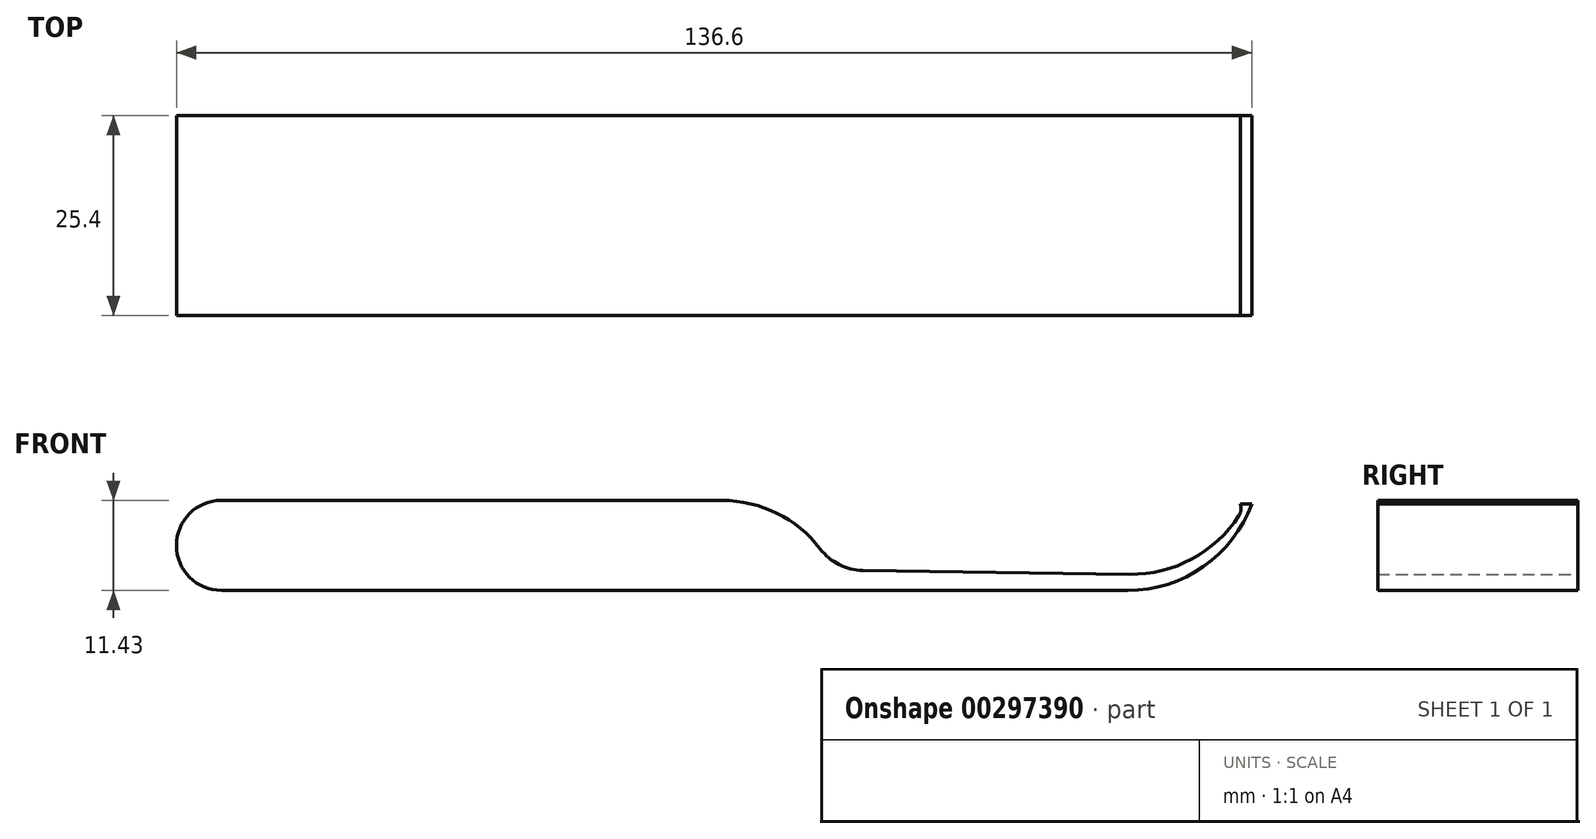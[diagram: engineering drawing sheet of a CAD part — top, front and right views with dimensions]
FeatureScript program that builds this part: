
annotation { "Feature Type Name" : "Feature", "Feature Type Description" : "" }
export const myFeature = defineFeature(function(context is Context, id is Id, definition is map)
    precondition{}
    {
        {
            var Q0;
            Q0=qCreatedBy(makeId("Front.planeOp"),FACE);
            var sketch = newSketch(context, id + "F0", { "sketchPlane" : qUnion([Q0])});
            skLineSegment(sketch, "E0", {"start": v(0, 11.43) * mm, "end": v(63.62, 11.43) * mm});
            skArc(sketch, "E1", {"start": v(76.07, 5.26) * mm, "mid": v(70.56, 9.8) * mm, "end": v(63.62, 11.43) * mm});
            skArc(sketch, "E2", {"start": v(76.07, 5.26) * mm, "mid": v(78.46, 3.28) * mm, "end": v(81.47, 2.54) * mm});
            skLineSegment(sketch, "E3", {"start": v(0, 0) * mm, "end": v(115.13, 0) * mm});
            skArc(sketch, "E4", {"start": v(115.13, 0) * mm, "mid": v(124.74, 3.02) * mm, "end": v(130.89, 11) * mm});
            skArc(sketch, "E5", {"start": v(115.35, 2.05) * mm, "mid": v(123.27, 3.98) * mm, "end": v(129.25, 9.52) * mm});
            skLineSegment(sketch, "E6", {"start": v(81.47, 2.54) * mm, "end": v(115.35, 2.05) * mm});
            skLineSegment(sketch, "E7", {"start": v(115.13, 16.78) * mm, "end": v(129.25, 9.52) * mm, "construction": true});
            skArc(sketch, "E8", {"start": v(129.25, 9.53) * mm, "mid": v(129.5, 10.24) * mm, "end": v(129.4, 11) * mm});
            skLineSegment(sketch, "E9", {"start": v(129.4, 11) * mm, "end": v(130.89, 11) * mm});
            skArc(sketch, "E10", {"start": v(0, 11.43) * mm, "mid": v(-5.72, 5.72) * mm, "end": v(0, 0) * mm});
            skSolve(sketch);
        }
        {
            var Q0;
            Q0=makeQuery(id+"F0.imprint","IMPRINT",FACE,{"disambiguationData":[TD([[makeQuery(id+"F0.imprint","IMPRINT",EDGE,{"derivedFrom":sQuery(id+"F0.wireOp",EDGE,"E0")}),-1.0]])]});
            extrude(context, id + "F1", {"entities" : qUnion([Q0]), "depth" : 25.4 * mm});
        }
    });
